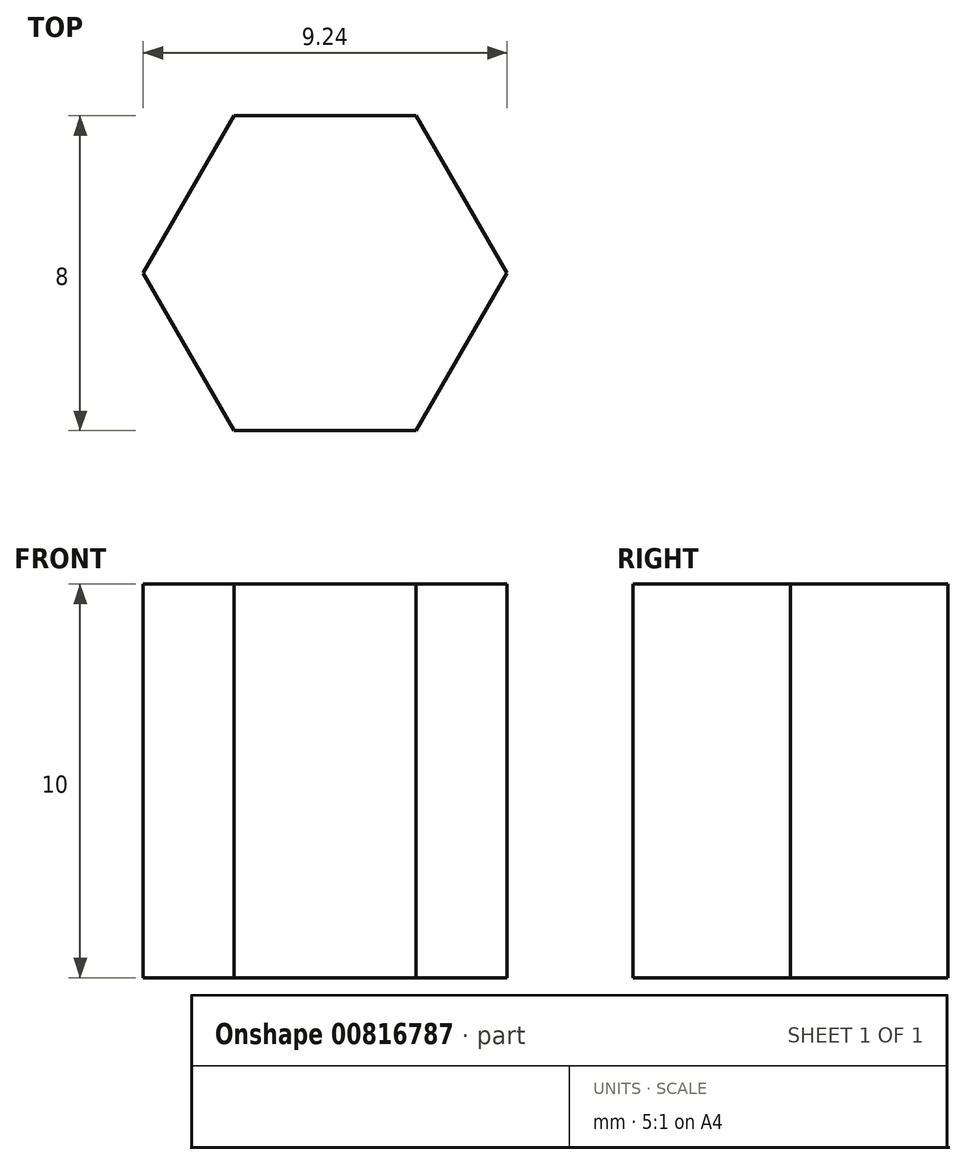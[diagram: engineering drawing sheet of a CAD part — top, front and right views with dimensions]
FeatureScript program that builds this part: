
annotation { "Feature Type Name" : "Feature", "Feature Type Description" : "" }
export const myFeature = defineFeature(function(context is Context, id is Id, definition is map)
    precondition{}
    {
        {
            var Q0;
            Q0=qCreatedBy(makeId("Top.planeOp"),FACE);
            var sketch = newSketch(context, id + "F0", { "sketchPlane" : qUnion([Q0])});
            skCircle(sketch, "E0.cCircle", {"center": v(0, 0) * mm, "radius": 4 * mm, "construction": true});
            skLineSegment(sketch, "E0.0", {"start": v(4.62, 0) * mm, "end": v(2.3, -4) * mm});
            skLineSegment(sketch, "E0.1", {"start": v(2.3, -4) * mm, "end": v(-2.3, -4) * mm});
            skLineSegment(sketch, "E0.2", {"start": v(-2.3, -4) * mm, "end": v(-4.62, 0) * mm});
            skLineSegment(sketch, "E0.3", {"start": v(-4.62, 0) * mm, "end": v(-2.3, 4) * mm});
            skLineSegment(sketch, "E0.4", {"start": v(-2.3, 4) * mm, "end": v(2.3, 4) * mm});
            skLineSegment(sketch, "E0.5", {"start": v(2.3, 4) * mm, "end": v(4.62, 0) * mm});
            skPoint(sketch, "E0.0.midPoint", {"position": v(3.46, -2) * mm});
            skSolve(sketch);
        }
        {
            var Q0;
            Q0 = qSketchRegion(id + "F0", true);
            extrude(context, id + "F1", {"entities" : qUnion([Q0]), "depth" : 10 * mm, "offsetDistance" : 25 * mm});
        }
    });
